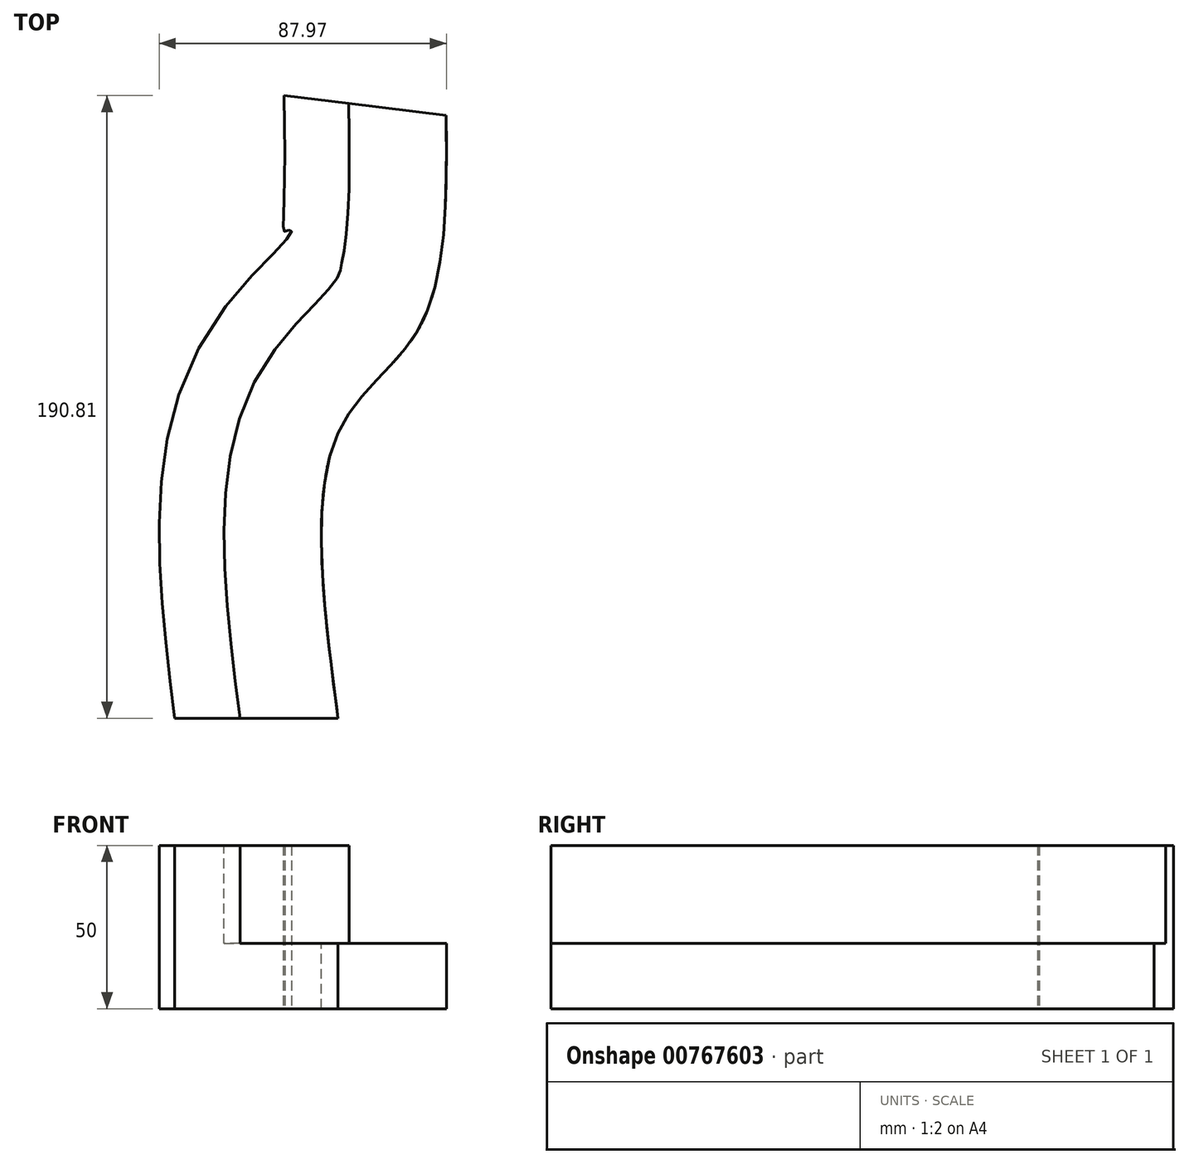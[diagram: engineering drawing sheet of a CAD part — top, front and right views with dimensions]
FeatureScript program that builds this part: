
annotation { "Feature Type Name" : "Feature", "Feature Type Description" : "" }
export const myFeature = defineFeature(function(context is Context, id is Id, definition is map)
    precondition{}
    {
        {
            var Q0;
            Q0=qCreatedBy(makeId("Front.planeOp"),FACE);
            var sketch = newSketch(context, id + "F0", { "sketchPlane" : qUnion([Q0])});
            skLineSegment(sketch, "E0.bottom", {"start": v(-50, 50) * mm, "end": v(-30, 50) * mm});
            skLineSegment(sketch, "E0.top", {"start": v(-50, 0) * mm, "end": v(-30, 0) * mm});
            skLineSegment(sketch, "E0.left", {"start": v(-50, 50) * mm, "end": v(-50, 0) * mm});
            skLineSegment(sketch, "E0.right", {"start": v(-30, 50) * mm, "end": v(-30, 20) * mm});
            skLineSegment(sketch, "E1.bottom", {"start": v(-30, 20) * mm, "end": v(0, 20) * mm});
            skLineSegment(sketch, "E1.top", {"start": v(-50, 0) * mm, "end": v(0, 0) * mm});
            skLineSegment(sketch, "E1.left", {"start": v(-50, 20) * mm, "end": v(-50, 0) * mm});
            skLineSegment(sketch, "E1.right", {"start": v(0, 20) * mm, "end": v(0, 0) * mm});
            skSolve(sketch);
        }
        {
            var Q0;
            Q0=qCreatedBy(makeId("Top.planeOp"),FACE);
            var sketch = newSketch(context, id + "F1", { "sketchPlane" : qUnion([Q0])});
            skFitSpline(sketch, "E2", {"points": [v(0, 0) * mm, v(0, 87.44) * mm, v(25.07, 119.97) * mm, v(33.13, 184.82) * mm], "startDerivative": vector(-33.75, 259.44) * mm, "endDerivative": vector(-2.05, 217.85) * mm});
            skSolve(sketch);
        }
        {
            var Q0;
            Q0=makeQuery(id+"F0.imprint","IMPRINT",FACE,{"disambiguationData":[TD([[makeQuery(id+"F0.imprint","IMPRINT",EDGE,{"derivedFrom":sQuery(id+"F0.wireOp",EDGE,"E0.bottom")}),-1.0]])]});
            var Q1;
            Q1=sQuery(id+"F1.wireOp",EDGE,"E2");
            sweep(context, id + "F2", {"profiles" : qUnion([Q0]), "path" : qUnion([Q1])});
        }
    });
